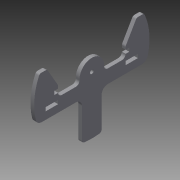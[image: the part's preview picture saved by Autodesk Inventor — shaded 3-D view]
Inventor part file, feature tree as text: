
AUTODESK INVENTOR PART (.ipt)
format: ipt  version: 2015 (Build 190159000, 159)  size: 174,592 bytes
history: native  units: mm
features: extrude x1
ambient origin geometry x8: Origin, YZ Plane, XZ Plane, XY Plane, X Axis, Y Axis, Z Axis, Center Point
bodies: Body1 (feature_tree)
feature tree (1):
  extrude  "Extrusion5"  Depth=94.0mm
